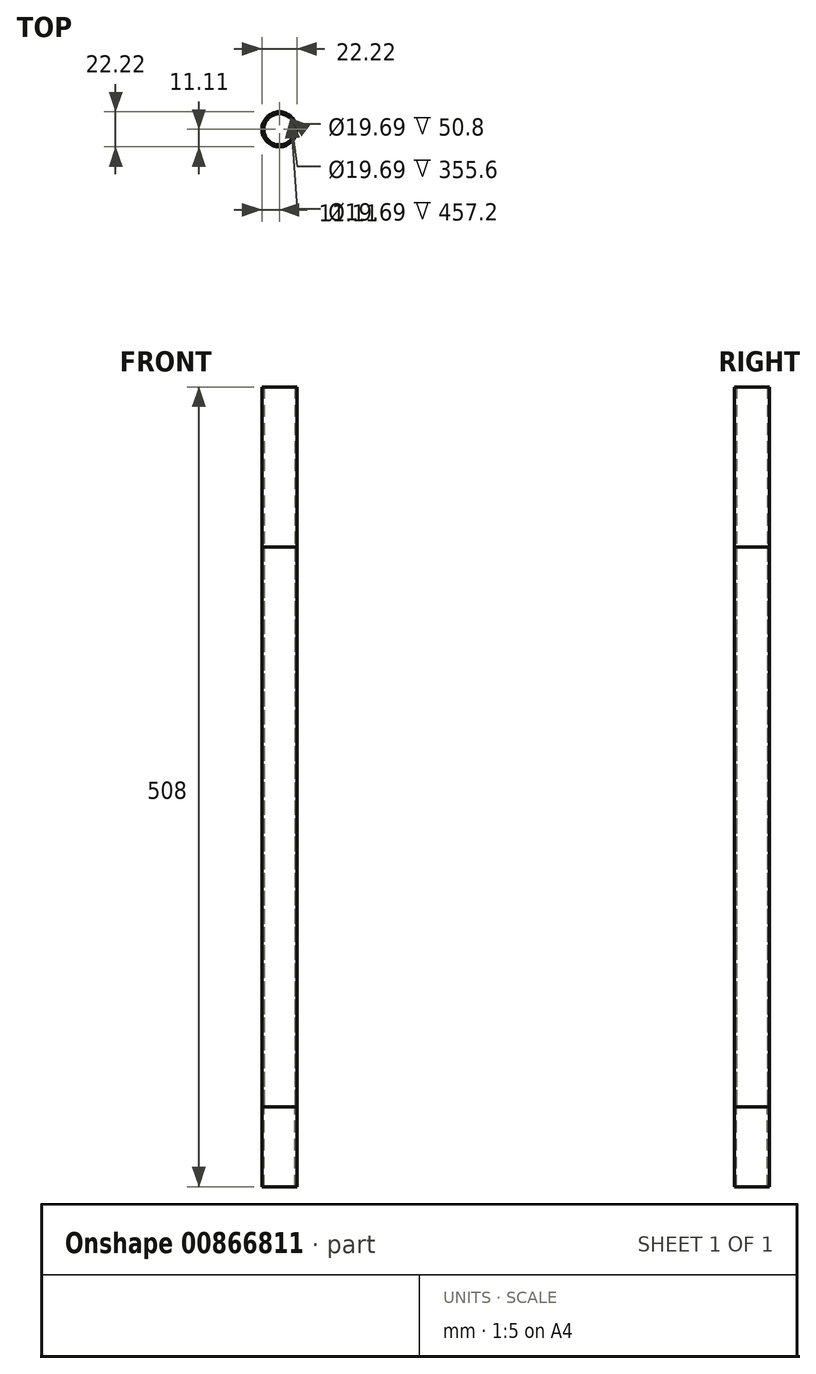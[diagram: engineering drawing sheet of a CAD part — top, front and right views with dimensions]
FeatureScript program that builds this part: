
annotation { "Feature Type Name" : "Feature", "Feature Type Description" : "" }
export const myFeature = defineFeature(function(context is Context, id is Id, definition is map)
    precondition{}
    {
        {
            var Q0;
            Q0=qCreatedBy(makeId("Top.planeOp"),FACE);
            var sketch = newSketch(context, id + "F0", { "sketchPlane" : qUnion([Q0])});
            skCircle(sketch, "E0", {"center": v(0, 0) * mm, "radius": 11.11 * mm});
            skCircle(sketch, "E1.0", {"center": v(0, 0) * mm, "radius": 9.84 * mm});
            skSolve(sketch);
        }
        {
            var Q0;
            Q0=makeQuery(id+"F0.imprint","IMPRINT",FACE,{"disambiguationData":[TD([[makeQuery(id+"F0.imprint","IMPRINT",EDGE,{"derivedFrom":sQuery(id+"F0.wireOp",EDGE,"E0")}),1.0]])]});
            extrude(context, id + "F1", {"entities" : qUnion([Q0]), "depth" : 457.2 * mm, "offsetDistance" : 25.4 * mm});
        }
        {
            var Q0;
            Q0=makeQuery(id+"F1.opExtrude","CAP_FACE",FACE,{"disambiguationData":[OSD([sQuery(id+"F0.wireOp",EDGE,"E0"),sQuery(id+"F0.wireOp",EDGE,"E1.0")])],"isStart":true});
            extrude(context, id + "F2", {"entities" : qUnion([Q0]), "depth" : 50.8 * mm, "offsetDistance" : 25.4 * mm});
        }
        {
            var Q0;
            Q0=makeQuery(id+"F0.imprint","IMPRINT",FACE,{"disambiguationData":[TD([[makeQuery(id+"F0.imprint","IMPRINT",EDGE,{"derivedFrom":sQuery(id+"F0.wireOp",EDGE,"E0")}),1.0]])]});
            extrude(context, id + "F3", {"entities" : qUnion([Q0]), "depth" : 355.6 * mm, "offsetDistance" : 25.4 * mm});
        }
    });
